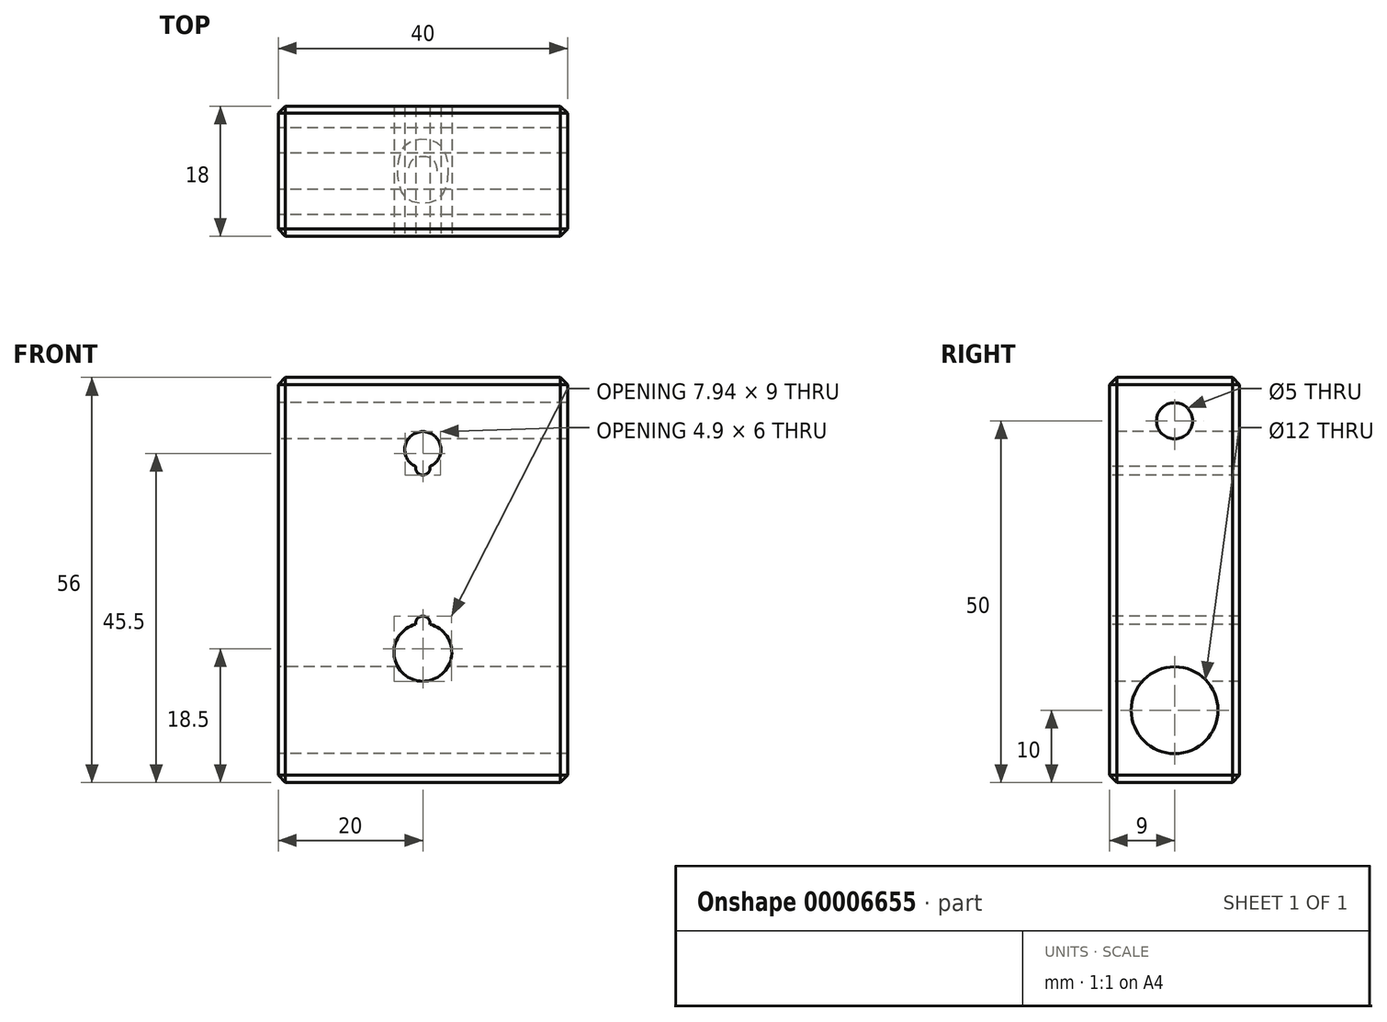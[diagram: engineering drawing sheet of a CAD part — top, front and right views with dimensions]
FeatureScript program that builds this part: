
annotation { "Feature Type Name" : "Feature", "Feature Type Description" : "" }
export const myFeature = defineFeature(function(context is Context, id is Id, definition is map)
    precondition{}
    {
        {
            var Q0;
            Q0=qCreatedBy(makeId("Right.planeOp"),FACE);
            var sketch = newSketch(context, id + "F0", { "sketchPlane" : qUnion([Q0])});
            skLineSegment(sketch, "E0.bottom", {"start": v(-9, 56) * mm, "end": v(9, 56) * mm});
            skLineSegment(sketch, "E0.top", {"start": v(-9, 0) * mm, "end": v(9, 0) * mm});
            skLineSegment(sketch, "E0.left", {"start": v(-9, 56) * mm, "end": v(-9, 0) * mm});
            skLineSegment(sketch, "E0.right", {"start": v(9, 56) * mm, "end": v(9, 0) * mm});
            skCircle(sketch, "E1", {"center": v(0, 50) * mm, "radius": 2.5 * mm});
            skCircle(sketch, "E2", {"center": v(0, 10) * mm, "radius": 6 * mm});
            skLineSegment(sketch, "E3", {"start": v(0, 56) * mm, "end": v(0, 0) * mm, "construction": true});
            skSolve(sketch);
        }
        {
            var Q0;
            Q0 = qSketchRegion(id + "F0", true);
            extrude(context, id + "F1", {"entities" : qUnion([Q0]), "depth" : 40 * mm});
        }
        {
            var Q0;
            Q0=makeQuery(id+"F1.opExtrude","SWEPT_FACE",FACE,{"disambiguationData":[OSD([sQuery(id+"F0.wireOp",EDGE,"E0.bottom")])]});
            var Q1;
            Q1=makeQuery(id+"F1.opExtrude","SWEPT_FACE",FACE,{"disambiguationData":[OSD([sQuery(id+"F0.wireOp",EDGE,"E0.top")])]});
            var Q2;
            Q2=makeQuery(id+"F1.opExtrude","SWEPT_FACE",FACE,{"disambiguationData":[OSD([sQuery(id+"F0.wireOp",EDGE,"E0.left")])]});
            var Q3;
            Q3=makeQuery(id+"F1.opExtrude","SWEPT_FACE",FACE,{"disambiguationData":[OSD([sQuery(id+"F0.wireOp",EDGE,"E0.right")])]});
            chamfer(context, id + "F2", {"entities" : qUnion([Q0, Q1, Q2, Q3]), "width" : 1 * mm, "tangentPropagation" : true});
        }
        {
            var Q0;
            Q0=makeQuery(id+"F1.opExtrude","SWEPT_FACE",FACE,{"disambiguationData":[OSD([sQuery(id+"F0.wireOp",EDGE,"E0.left")])]});
            var sketch = newSketch(context, id + "F3", { "sketchPlane" : qUnion([Q0])});
            skLineSegment(sketch, "E4.0", {"start": v(0, 52.5) * mm, "end": v(0, 47.5) * mm, "construction": true});
            skLineSegment(sketch, "E5.0", {"start": v(0, 16) * mm, "end": v(0, 4) * mm, "construction": true});
            skLineSegment(sketch, "E6", {"start": v(20, 55) * mm, "end": v(20, 1) * mm, "construction": true});
            skCircle(sketch, "E7", {"center": v(20, 46) * mm, "radius": 2.5 * mm});
            skCircle(sketch, "E8", {"center": v(20, 18) * mm, "radius": 4 * mm});
            skPoint(sketch, "E9", {"position": v(20, 14) * mm});
            skPoint(sketch, "E10", {"position": v(20, 48.5) * mm});
            skSolve(sketch);
        }
        {
            var Q0;
            Q0 = qSketchRegion(id + "F3", true);
            extrude(context, id + "F4", {"entities" : qUnion([Q0]), "operationType" : NewBodyOperationType.REMOVE, "oppositeDirection" : true, "depth" : 25 * mm});
        }
        {
            var Q0;
            Q0=makeQuery(id+"F1.opExtrude","SWEPT_FACE",FACE,{"disambiguationData":[OSD([sQuery(id+"F0.wireOp",EDGE,"E0.left")])]});
            var sketch = newSketch(context, id + "F5", { "sketchPlane" : qUnion([Q0])});
            skCircle(sketch, "E11.0", {"center": v(20, 46) * mm, "radius": 2.5 * mm, "construction": true});
            skCircle(sketch, "E12.0", {"center": v(20, 18) * mm, "radius": 4 * mm, "construction": true});
            skCircle(sketch, "E13", {"center": v(20, 43.5) * mm, "radius": 1 * mm});
            skCircle(sketch, "E14", {"center": v(20, 22) * mm, "radius": 1 * mm});
            skSolve(sketch);
        }
        {
            var Q0;
            Q0 = qSketchRegion(id + "F5", true);
            extrude(context, id + "F6", {"entities" : qUnion([Q0]), "operationType" : NewBodyOperationType.REMOVE, "oppositeDirection" : true, "depth" : 25 * mm});
        }
    });
